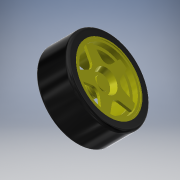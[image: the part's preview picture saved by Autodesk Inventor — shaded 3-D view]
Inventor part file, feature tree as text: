
AUTODESK INVENTOR PART (.ipt)
format: ipt  version: 2019 (Build 230136000, 136)  size: 333,312 bytes
history: native  units: mm
features: sketch x5, revolve x3, extrude x2, plane x1, direct_edit x1, projected_geometry x1, other x1
ambient origin geometry x8: Origin, YZ Plane, XZ Plane, XY Plane, X Axis, Y Axis, Z Axis, Center Point
bodies: Solid1 (feature_tree)
feature tree (14):
  revolve  "Revolution1"  [1 undecoded]
  extrude  "Extrusion2"  Depth=15.0mm
  extrude  "Extrusion3"  Depth=7.5mm
  plane  "Work Plane1"
  revolve  "Revolution2"  [1 undecoded]
  revolve  "Revolution3"  [1 undecoded]
  direct_edit  "Direct Edit1"
  sketch  "Sketch1"  dims[d0=90.0deg d2=11.3mm]
  sketch  "Sketch3"  dims[d3=52.0mm d4=15.0mm]
  projected_geometry  "Projected Loop2"
  sketch  "Sketch4"  dims[d5=3.0mm d6=7.5mm]
  sketch  "Sketch5"  dims[d7=25.8mm d8=21.0mm]
  sketch  "Sketch6"  dims[d9=1.0mm d10=18.2mm d11=3.0mm d12=1.2mm d13=0.5mm d14=10.0mm d15=1.5mm d16=5.0mm d17=30.2mm d18=18.0mm d19=2.0mm d20=41.0mm d23=2.0mm d24=3.0mm d25=21.5mm d26=50.0mm d28=360.0deg d30=23.5mm d31=5.5mm d32=2.0mm d33=0.0mm d34=5.2mm d35=3.65mm d36=2.6mm d37=13.0mm d38=0.0mm d39=90.0deg d40=2.0mm d41=2.0mm d42=2.0mm d43=90.0deg d44=65.0mm d45=2.5mm d46=0.1mm d47=0.1mm d48=90.0deg d49=9.0mm d50=10.0mm d51=10.0mm]
  other  "Scale1"
note: 3 required parameter values undecoded (feature->parameter linkage not recoverable at this tier; creation-order binding heuristic only, values carry confidence <= 0.55)
